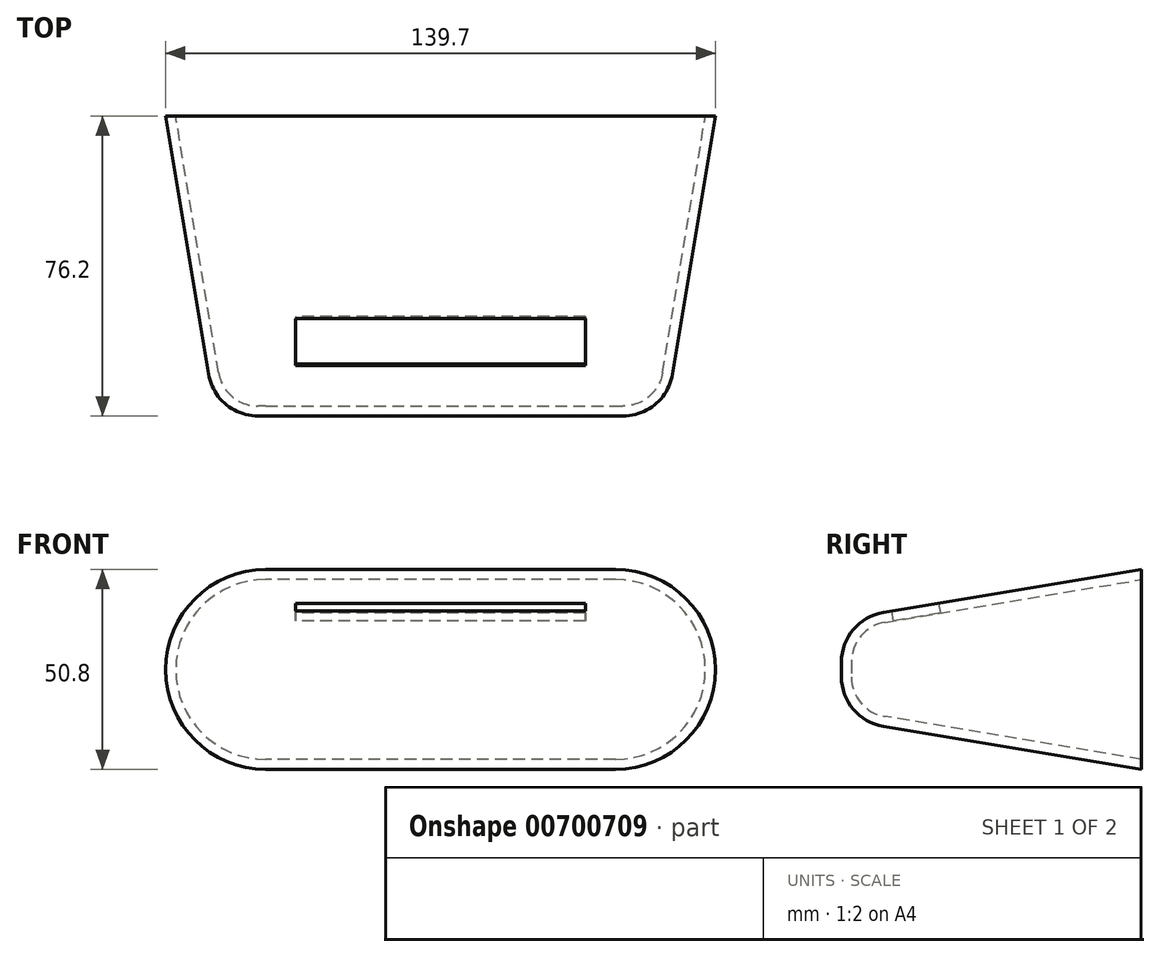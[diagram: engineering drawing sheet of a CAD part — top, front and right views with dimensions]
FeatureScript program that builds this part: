
annotation { "Feature Type Name" : "Feature", "Feature Type Description" : "" }
export const myFeature = defineFeature(function(context is Context, id is Id, definition is map)
    precondition{}
    {
        {
            var Q0;
            Q0=qCreatedBy(makeId("Front.planeOp"),FACE);
            var sketch = newSketch(context, id + "F0", { "sketchPlane" : qUnion([Q0])});
            skLineSegment(sketch, "E0.bottom", {"start": v(82.55, 38.1) * mm, "end": v(-82.55, 38.1) * mm});
            skLineSegment(sketch, "E0.top", {"start": v(82.55, -38.1) * mm, "end": v(-82.55, -38.1) * mm});
            skLineSegment(sketch, "E0.left", {"start": v(82.55, 38.1) * mm, "end": v(82.55, -38.1) * mm});
            skLineSegment(sketch, "E0.right", {"start": v(-82.55, 38.1) * mm, "end": v(-82.55, -38.1) * mm});
            skPoint(sketch, "E0.middle", {"position": v(0, 0) * mm});
            skSolve(sketch);
        }
        {
            var Q0;
            Q0=makeQuery(id+"F0.imprint","IMPRINT",FACE,{"disambiguationData":[TD([[makeQuery(id+"F0.imprint","IMPRINT",EDGE,{"derivedFrom":sQuery(id+"F0.wireOp",EDGE,"E0.bottom")}),1.0]])]});
            extrude(context, id + "F1", {"entities" : qUnion([Q0]), "oppositeDirection" : true, "depth" : 76.2 * mm, "offsetDistance" : 25.4 * mm});
        }
        {
            var Q0;
            Q0=makeQuery(id+"F1.opExtrude","SWEPT_EDGE",EDGE,{"disambiguationData":[OSD([sQuery(id+"F0.wireOp",EDGE,"E0.bottom"),sQuery(id+"F0.wireOp",EDGE,"E0.left")])]});
            var Q1;
            Q1=makeQuery(id+"F1.opExtrude","SWEPT_EDGE",EDGE,{"disambiguationData":[OSD([sQuery(id+"F0.wireOp",EDGE,"E0.top"),sQuery(id+"F0.wireOp",EDGE,"E0.left")])]});
            var Q2;
            Q2=makeQuery(id+"F1.opExtrude","SWEPT_EDGE",EDGE,{"disambiguationData":[OSD([sQuery(id+"F0.wireOp",EDGE,"E0.top"),sQuery(id+"F0.wireOp",EDGE,"E0.right")])]});
            var Q3;
            Q3=makeQuery(id+"F1.opExtrude","SWEPT_EDGE",EDGE,{"disambiguationData":[OSD([sQuery(id+"F0.wireOp",EDGE,"E0.bottom"),sQuery(id+"F0.wireOp",EDGE,"E0.right")])]});
            fillet(context, id + "F2", {"entities" : qUnion([Q0, Q1, Q2, Q3]), "radius" : 38.1 * mm, "tangentPropagation" : true, "allowEdgeOverflow" : false});
        }
        {
            var Q0;
            Q0=makeQuery(id+"F1.opExtrude","CAP_EDGE",EDGE,{"disambiguationData":[OSD([sQuery(id+"F0.wireOp",EDGE,"E0.bottom")])],"isStart":true});
            chamfer(context, id + "F3", {"entities" : qUnion([Q0]), "chamferType" : ChamferType.TWO_OFFSETS, "width1" : 25.4 * mm, "oppositeDirection" : false, "width2" : 152.4 * mm, "tangentPropagation" : true});
        }
        {
            var Q0;
            Q0=makeQuery(id+"F3.opChamfer","BLEND_FACE",FACE,{"disambiguationData":[OSD([sQuery(id+"F0.wireOp",EDGE,"E0.bottom")])]});
            var sketch = newSketch(context, id + "F4", { "sketchPlane" : qUnion([Q0])});
            skLineSegment(sketch, "E1.bottom", {"start": v(36.83, 27.23) * mm, "end": v(-36.83, 27.23) * mm});
            skLineSegment(sketch, "E1.top", {"start": v(36.83, 15.04) * mm, "end": v(-36.83, 15.04) * mm});
            skLineSegment(sketch, "E1.left", {"start": v(36.83, 27.23) * mm, "end": v(36.83, 15.04) * mm});
            skLineSegment(sketch, "E1.right", {"start": v(-36.83, 27.23) * mm, "end": v(-36.83, 15.04) * mm});
            skPoint(sketch, "E1.middle", {"position": v(0, 21.14) * mm});
            skSolve(sketch);
        }
        {
            var Q0;
            {var subQ0=sQuery(id+"F0.wireOp",EDGE,"E0.bottom");Q0=makeQuery(id+"F3.opChamfer","BLEND_EDGE",EDGE,{"blendedFrom":[makeQuery(id+"F1.opExtrude","CAP_EDGE",EDGE,{"disambiguationData":[OSD([subQ0])],"isStart":true}),makeQuery(id+"F1.opExtrude","CAP_FACE",FACE,{"disambiguationData":[OSD([subQ0,sQuery(id+"F0.wireOp",EDGE,"E0.top"),sQuery(id+"F0.wireOp",EDGE,"E0.left"),sQuery(id+"F0.wireOp",EDGE,"E0.right")])],"isStart":true})],"blendedInto":[makeQuery(id+"F1.opExtrude","CAP_FACE",FACE,{"disambiguationData":[OSD([subQ0,sQuery(id+"F0.wireOp",EDGE,"E0.top"),sQuery(id+"F0.wireOp",EDGE,"E0.left"),sQuery(id+"F0.wireOp",EDGE,"E0.right")])],"isStart":true})]});}
            fillet(context, id + "F5", {"entities" : qUnion([Q0]), "radius" : 12.7 * mm, "tangentPropagation" : true, "allowEdgeOverflow" : false});
        }
        {
            var Q0;
            Q0=makeQuery(id+"F1.opExtrude","CAP_FACE",FACE,{"disambiguationData":[OSD([sQuery(id+"F0.wireOp",EDGE,"E0.bottom"),sQuery(id+"F0.wireOp",EDGE,"E0.top"),sQuery(id+"F0.wireOp",EDGE,"E0.left"),sQuery(id+"F0.wireOp",EDGE,"E0.right")])],"isStart":false});
            shell(context, id + "F6", {"entities" : qUnion([Q0]), "thickness" : 2.54 * mm});
        }
        {
            var Q0;
            Q0=qSketchRegion(id+"F4",true);
            extrude(context, id + "F7", {"entities" : qUnion([Q0]), "operationType" : NewBodyOperationType.REMOVE, "endBound" : BoundingType.UP_TO_NEXT, "oppositeDirection" : true, "depth" : 25.4 * mm, "offsetDistance" : 25.4 * mm});
        }
    });
